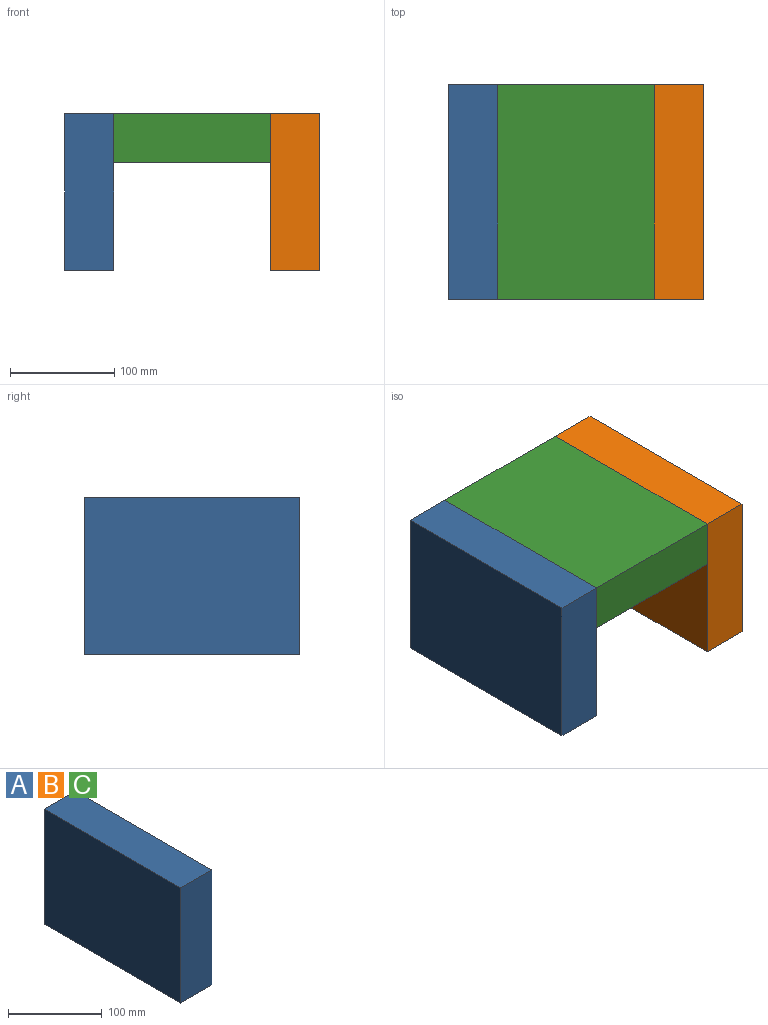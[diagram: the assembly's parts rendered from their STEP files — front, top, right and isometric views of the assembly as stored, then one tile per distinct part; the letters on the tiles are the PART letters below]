
ASSEMBLY  parts=3 mates=8
PART A: 6 faces, bbox 47x206x150 mm
  f0: plane 206x47mm, normal (0,0,-1), area 9682mm2, adj f1,f3,f4,f5
  f1: plane 206x150mm, normal (1,0,0), area 30900mm2, adj f0,f2,f4,f5
  f2: plane 206x47mm, normal (0,0,1), area 9682mm2, adj f1,f3,f4,f5
  f3: plane 206x150mm, normal (-1,0,0), area 30900mm2, adj f0,f2,f4,f5
  f4: plane 150x47mm, normal (0,-1,0), area 7050mm2, adj f0,f1,f2,f3
  f5: plane 150x47mm, normal (0,1,0), area 7050mm2, adj f0,f1,f2,f3
PART B: same geometry as A
PART C: same geometry as A
PLACE A t=(-210.35,-90.42,74.85)mm fixed
PLACE B t=(-13.35,-90.42,74.85)mm
PLACE C rot(axis=(0,-1,0),90deg) t=(-111.85,-90.42,126.35)mm
MATE parallel A.f4 <-> B.f4  axis (0,-1,0) through (-210.35,-296.42,74.85)mm
MATE planar A.f4 <-> B.f4  axis (0,-1,0) through (-210.35,-296.42,74.85)mm
MATE planar B.f3 <-> C.f0  axis (-1,0,0) through (-36.85,-193.42,74.85)mm
MATE planar C.f2 <-> A.f1  axis (-1,0,0) through (-186.85,-193.42,126.35)mm
MATE planar B.f4 <-> C.f4  axis (0,-1,0) through (-13.35,-296.42,74.85)mm
MATE planar C.f4 <-> A.f4  axis (0,-1,0) through (-111.85,-296.42,102.85)mm
MATE planar A.f2 <-> B.f2  axis (0,0,1) through (-210.35,-193.42,149.85)mm
MATE planar C.f1 <-> A.f2  axis (0,0,1) through (-111.85,-193.42,149.85)mm
